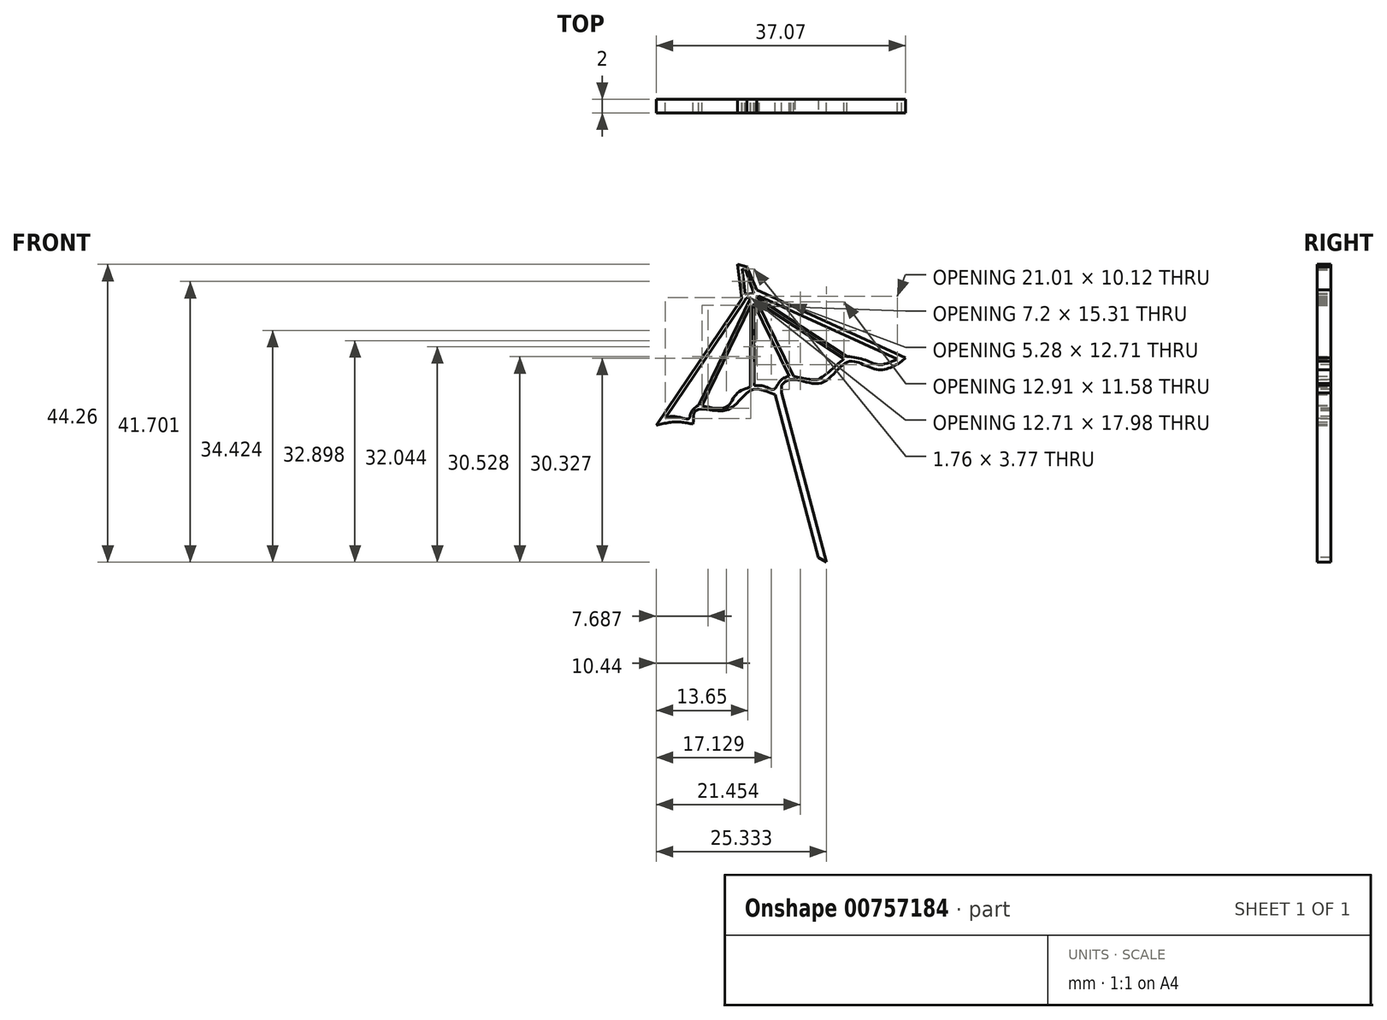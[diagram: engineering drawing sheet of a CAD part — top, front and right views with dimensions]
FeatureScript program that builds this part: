
annotation { "Feature Type Name" : "Feature", "Feature Type Description" : "" }
export const myFeature = defineFeature(function(context is Context, id is Id, definition is map)
    precondition{}
    {
        {
            var Q0;
            Q0=qCreatedBy(makeId("Front.planeOp"),FACE);
            var sketch = newSketch(context, id + "F0", { "sketchPlane" : qUnion([Q0])});
            skLineSegment(sketch, "E0", {"start": v(46.65, 4.58) * mm, "end": v(38.95, 33.58) * mm});
            skFitSpline(sketch, "E1", {"points": [v(38.95, 33.58) * mm, v(41.3, 35.83) * mm, v(45.9, 35.36) * mm, v(49.89, 38.5) * mm, v(54.14, 37.33) * mm, v(57.8, 38.55) * mm], "startDerivative": vector(10.96, 18.02) * mm, "endDerivative": vector(18.46, 11.33) * mm});
            skLineSegment(sketch, "E2", {"start": v(57.8, 38.55) * mm, "end": v(36.62, 48.18) * mm});
            skLineSegment(sketch, "E3", {"start": v(36.62, 48.18) * mm, "end": v(36.12, 48.12) * mm});
            skLineSegment(sketch, "E4", {"start": v(34.04, 47.85) * mm, "end": v(21.3, 29) * mm});
            skFitSpline(sketch, "E5", {"points": [v(38.95, 33.58) * mm, v(35.31, 34.23) * mm, v(31.88, 31.35) * mm, v(27.29, 31.3) * mm, v(26.8, 29.22) * mm], "startDerivative": vector(-15.38, 6.74) * mm, "endDerivative": vector(-0.78, -13.26) * mm});
            skFitSpline(sketch, "E6", {"points": [v(21.3, 29) * mm, v(24.2, 29.54) * mm, v(26.8, 29.22) * mm], "startDerivative": vector(5.51, 1.71) * mm, "endDerivative": vector(5.29, -1.1) * mm});
            skLineSegment(sketch, "E7", {"start": v(27.63, 32.02) * mm, "end": v(35.33, 48.02) * mm});
            skLineSegment(sketch, "E8", {"start": v(35.33, 46.89) * mm, "end": v(35.31, 34.76) * mm});
            skLineSegment(sketch, "E9", {"start": v(41.3, 35.83) * mm, "end": v(35.78, 47.1) * mm});
            skLineSegment(sketch, "E10", {"start": v(49.2, 38.94) * mm, "end": v(36.3, 47.39) * mm});
            skLineSegment(sketch, "E11", {"start": v(34.04, 47.85) * mm, "end": v(33.38, 52.96) * mm});
            skLineSegment(sketch, "E12", {"start": v(33.38, 52.96) * mm, "end": v(34.8, 52.59) * mm});
            skLineSegment(sketch, "E13", {"start": v(34.8, 52.59) * mm, "end": v(36.21, 49.17) * mm});
            skLineSegment(sketch, "E14.0", {"start": v(47.61, 4.84) * mm, "end": v(39.92, 33.83) * mm});
            skLineSegment(sketch, "E15", {"start": v(46.65, 4.58) * mm, "end": v(47.61, 4.84) * mm});
            skLineSegment(sketch, "E16", {"start": v(39.92, 33.83) * mm, "end": v(39.92, 35) * mm});
            skLineSegment(sketch, "E17.0", {"start": v(34.46, 47.57) * mm, "end": v(22.62, 30.08) * mm});
            skLineSegment(sketch, "E18", {"start": v(34.46, 47.57) * mm, "end": v(34.63, 47.92) * mm});
            skLineSegment(sketch, "E19", {"start": v(34.55, 48.51) * mm, "end": v(34.06, 52.29) * mm});
            skLineSegment(sketch, "E20", {"start": v(34.06, 52.29) * mm, "end": v(34.58, 52.12) * mm});
            skLineSegment(sketch, "E21", {"start": v(34.58, 52.12) * mm, "end": v(35.82, 48.68) * mm});
            skLineSegment(sketch, "E22", {"start": v(35.82, 48.68) * mm, "end": v(34.55, 48.51) * mm});
            skFitSpline(sketch, "E23", {"points": [v(22.62, 30.08) * mm, v(24.2, 30.35) * mm, v(26.16, 30.03) * mm, v(26.43, 30.89) * mm, v(27.26, 31.81) * mm, v(27.63, 32.02) * mm], "startDerivative": vector(6.08, 2.42) * mm, "endDerivative": vector(3.97, 0.03) * mm});
            skFitSpline(sketch, "E24", {"points": [v(27.63, 32.02) * mm, v(29.97, 31.6) * mm, v(31.67, 31.74) * mm, v(32.43, 32.43) * mm, v(32.9, 33.3) * mm, v(33.82, 34.16) * mm, v(34.77, 34.55) * mm, v(35.31, 34.76) * mm], "startDerivative": vector(11.82, -2.03) * mm, "endDerivative": vector(4.38, 3.05) * mm});
            skLineSegment(sketch, "E25", {"start": v(35.89, 34.95) * mm, "end": v(35.78, 47.1) * mm});
            skFitSpline(sketch, "E26", {"points": [v(35.89, 34.95) * mm, v(37.59, 34.76) * mm, v(38.75, 34.38) * mm, v(39.62, 35.51) * mm, v(41.06, 36.32) * mm], "startDerivative": vector(6.59, 0.3) * mm, "endDerivative": vector(7.55, 1.09) * mm});
            skLineSegment(sketch, "E27", {"start": v(28.13, 31.92) * mm, "end": v(35.33, 46.89) * mm});
            skLineSegment(sketch, "E28", {"start": v(41.91, 35.83) * mm, "end": v(36.3, 47.39) * mm});
            skFitSpline(sketch, "E29", {"points": [v(41.68, 36.32) * mm, v(44.73, 35.8) * mm, v(45.64, 35.99) * mm, v(47.58, 37.54) * mm, v(49.2, 38.94) * mm], "startDerivative": vector(11.68, -2.29) * mm, "endDerivative": vector(6.07, 5.3) * mm});
            skLineSegment(sketch, "E30", {"start": v(50.8, 38.5) * mm, "end": v(36.12, 48.12) * mm});
            skFitSpline(sketch, "E31", {"points": [v(49.65, 39.27) * mm, v(51.7, 38.94) * mm, v(53.44, 38.27) * mm, v(54.74, 38.05) * mm, v(57.13, 38.85) * mm], "startDerivative": vector(8.03, -0.77) * mm, "endDerivative": vector(9.01, 3.82) * mm});
            skLineSegment(sketch, "E32", {"start": v(57.8, 38.55) * mm, "end": v(58.36, 39.09) * mm});
            skLineSegment(sketch, "E33", {"start": v(58.36, 39.09) * mm, "end": v(36.21, 49.17) * mm});
            skLineSegment(sketch, "E34.trimOffspring", {"start": v(35.33, 48.02) * mm, "end": v(34.63, 47.92) * mm});
            skSolve(sketch);
        }
        {
            var Q0;
            Q0 = qSketchRegion(id + "F0", true);
            extrude(context, id + "F1", {"entities" : qUnion([Q0]), "depth" : 2 * mm, "offsetDistance" : 25 * mm});
        }
        {
            var Q0;
            Q0=makeQuery(id+"F1.opExtrude","SWEPT_EDGE",EDGE,{"disambiguationData":[OSD([sQuery(id+"F0.wireOp",EDGE,"E0"),sQuery(id+"F0.wireOp",EDGE,"E15")])]});
            chamfer(context, id + "F2", {"entities" : qUnion([Q0]), "width" : 5 * mm, "tangentPropagation" : true});
        }
    });
